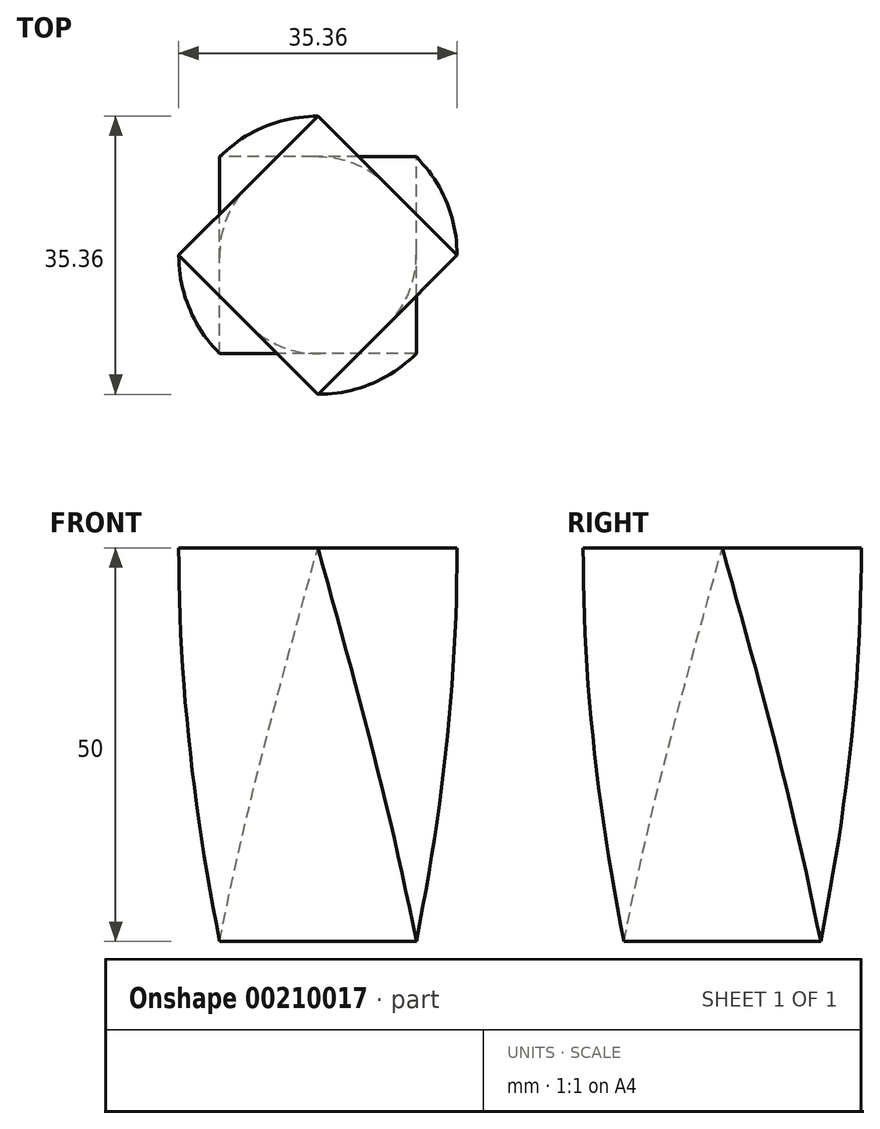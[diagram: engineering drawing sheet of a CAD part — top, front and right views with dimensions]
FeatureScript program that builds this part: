
annotation { "Feature Type Name" : "Feature", "Feature Type Description" : "" }
export const myFeature = defineFeature(function(context is Context, id is Id, definition is map)
    precondition{}
    {
        {
            assignVariable(context, id + "F0", {"name" : "p", "anyValue" : 10});
        }
        {
            var Q0;
            Q0=qCreatedBy(makeId("Top.planeOp"),FACE);
            cPlane(context, id + "F1", {"entities" : qUnion([Q0]), "cplaneType" : CPlaneType.OFFSET, "offset" : (getVariable(context, 'p')) * mm, "width" : 150 * mm, "height" : 150 * mm});
        }
        {
            var Q0;
            Q0=qCreatedBy(id+"F1.planeOp",FACE);
            cPlane(context, id + "F2", {"entities" : qUnion([Q0]), "cplaneType" : CPlaneType.OFFSET, "offset" : (getVariable(context, 'p')) * mm, "width" : 150 * mm, "height" : 150 * mm});
        }
        {
            var Q0;
            Q0=qCreatedBy(id+"F2.planeOp",FACE);
            cPlane(context, id + "F3", {"entities" : qUnion([Q0]), "cplaneType" : CPlaneType.OFFSET, "offset" : (getVariable(context, 'p')) * mm, "width" : 150 * mm, "height" : 150 * mm});
        }
        {
            var Q0;
            Q0=qCreatedBy(id+"F3.planeOp",FACE);
            cPlane(context, id + "F4", {"entities" : qUnion([Q0]), "cplaneType" : CPlaneType.OFFSET, "offset" : (getVariable(context, 'p')) * mm, "width" : 150 * mm, "height" : 150 * mm});
        }
        {
            var Q0;
            Q0=qCreatedBy(id+"F4.planeOp",FACE);
            cPlane(context, id + "F5", {"entities" : qUnion([Q0]), "cplaneType" : CPlaneType.OFFSET, "offset" : (getVariable(context, 'p')) * mm, "width" : 150 * mm, "height" : 150 * mm});
        }
        {
            var Q0;
            Q0=qCreatedBy(makeId("Top.planeOp"),FACE);
            var sketch = newSketch(context, id + "F6", { "sketchPlane" : qUnion([Q0])});
            skLineSegment(sketch, "E0.bottom", {"start": v(12.5, -12.5) * mm, "end": v(-12.5, -12.5) * mm});
            skLineSegment(sketch, "E0.top", {"start": v(12.5, 12.5) * mm, "end": v(-12.5, 12.5) * mm});
            skLineSegment(sketch, "E0.left", {"start": v(12.5, -12.5) * mm, "end": v(12.5, 12.5) * mm});
            skLineSegment(sketch, "E0.right", {"start": v(-12.5, -12.5) * mm, "end": v(-12.5, 12.5) * mm});
            skPoint(sketch, "E0.middle", {"position": v(0, 0) * mm});
            skSolve(sketch);
        }
        {
            var Q0;
            Q0=qCreatedBy(id+"F1.planeOp",FACE);
            var sketch = newSketch(context, id + "F7", { "sketchPlane" : qUnion([Q0])});
            skPoint(sketch, "E1.middle", {"position": v(0, 0) * mm});
            skLineSegment(sketch, "E2.1.1", {"start": v(10.4, -14.3) * mm, "end": v(-14.3, -10.4) * mm});
            skLineSegment(sketch, "E2.1.2", {"start": v(14.3, 10.4) * mm, "end": v(-10.4, 14.3) * mm});
            skLineSegment(sketch, "E2.1.3", {"start": v(10.4, -14.3) * mm, "end": v(14.3, 10.4) * mm});
            skLineSegment(sketch, "E2.1.4", {"start": v(-14.3, -10.4) * mm, "end": v(-10.4, 14.3) * mm});
            skSolve(sketch);
        }
        {
            var Q0;
            Q0=qCreatedBy(id+"F2.planeOp",FACE);
            var sketch = newSketch(context, id + "F8", { "sketchPlane" : qUnion([Q0])});
            skPoint(sketch, "E3.middle", {"position": v(0, 0) * mm});
            skLineSegment(sketch, "E4.1.0", {"start": v(15.75, 8.03) * mm, "end": v(-8.03, 15.75) * mm});
            skLineSegment(sketch, "E4.1.1", {"start": v(8.03, -15.75) * mm, "end": v(-15.75, -8.03) * mm});
            skLineSegment(sketch, "E4.1.2", {"start": v(8.03, -15.75) * mm, "end": v(15.75, 8.03) * mm});
            skLineSegment(sketch, "E4.1.3", {"start": v(-15.75, -8.03) * mm, "end": v(-8.03, 15.75) * mm});
            skSolve(sketch);
        }
        {
            var Q0;
            Q0=qCreatedBy(id+"F3.planeOp",FACE);
            var sketch = newSketch(context, id + "F9", { "sketchPlane" : qUnion([Q0])});
            skPoint(sketch, "E5.middle", {"position": v(0, 0) * mm});
            skLineSegment(sketch, "E6.1.0", {"start": v(16.81, 5.46) * mm, "end": v(-5.46, 16.81) * mm});
            skLineSegment(sketch, "E6.1.1", {"start": v(5.46, -16.81) * mm, "end": v(16.81, 5.46) * mm});
            skLineSegment(sketch, "E6.1.2", {"start": v(5.46, -16.81) * mm, "end": v(-16.81, -5.46) * mm});
            skLineSegment(sketch, "E6.1.4", {"start": v(-16.81, -5.46) * mm, "end": v(-5.46, 16.81) * mm});
            skSolve(sketch);
        }
        {
            var Q0;
            Q0=qCreatedBy(id+"F4.planeOp",FACE);
            var sketch = newSketch(context, id + "F10", { "sketchPlane" : qUnion([Q0])});
            skPoint(sketch, "E7.middle", {"position": v(0, 0) * mm});
            skLineSegment(sketch, "E8.1.0", {"start": v(2.77, -17.46) * mm, "end": v(17.46, 2.77) * mm});
            skLineSegment(sketch, "E8.1.1", {"start": v(17.46, 2.77) * mm, "end": v(-2.77, 17.46) * mm});
            skLineSegment(sketch, "E8.1.2", {"start": v(-17.46, -2.77) * mm, "end": v(-2.77, 17.46) * mm});
            skLineSegment(sketch, "E8.1.3", {"start": v(2.77, -17.46) * mm, "end": v(-17.46, -2.77) * mm});
            skSolve(sketch);
        }
        {
            var Q0;
            Q0=qCreatedBy(id+"F5.planeOp",FACE);
            var sketch = newSketch(context, id + "F11", { "sketchPlane" : qUnion([Q0])});
            skPoint(sketch, "E9.middle", {"position": v(0, 0) * mm});
            skLineSegment(sketch, "E10.1.0", {"start": v(-17.68, 0) * mm, "end": v(0, 17.68) * mm});
            skLineSegment(sketch, "E10.1.2", {"start": v(0, -17.68) * mm, "end": v(-17.68, 0) * mm});
            skLineSegment(sketch, "E10.1.3", {"start": v(17.68, 0) * mm, "end": v(0, 17.68) * mm});
            skLineSegment(sketch, "E10.1.4", {"start": v(0, -17.68) * mm, "end": v(17.68, 0) * mm});
            skSolve(sketch);
        }
        {
            var Q0;
            Q0=makeQuery(id+"F6.imprint","IMPRINT",FACE,{"disambiguationData":[TD([[makeQuery(id+"F6.imprint","IMPRINT",EDGE,{"derivedFrom":sQuery(id+"F6.wireOp",EDGE,"E0.bottom")}),-1.0]])]});
            var Q1;
            Q1=makeQuery(id+"F7.imprint","IMPRINT",FACE,{"disambiguationData":[TD([[makeQuery(id+"F7.imprint","IMPRINT",EDGE,{"derivedFrom":sQuery(id+"F7.wireOp",EDGE,"E2.1.1")}),-1.0]])]});
            var Q2;
            Q2=makeQuery(id+"F8.imprint","IMPRINT",FACE,{"disambiguationData":[TD([[makeQuery(id+"F8.imprint","IMPRINT",EDGE,{"derivedFrom":sQuery(id+"F8.wireOp",EDGE,"E4.1.0")}),1.0]])]});
            var Q3;
            Q3=makeQuery(id+"F9.imprint","IMPRINT",FACE,{"disambiguationData":[TD([[makeQuery(id+"F9.imprint","IMPRINT",EDGE,{"derivedFrom":sQuery(id+"F9.wireOp",EDGE,"E6.1.0")}),1.0]])]});
            var Q4;
            Q4=makeQuery(id+"F10.imprint","IMPRINT",FACE,{"disambiguationData":[TD([[makeQuery(id+"F10.imprint","IMPRINT",EDGE,{"derivedFrom":sQuery(id+"F10.wireOp",EDGE,"E8.1.0")}),1.0]])]});
            var Q5;
            Q5=makeQuery(id+"F11.imprint","IMPRINT",FACE,{"disambiguationData":[TD([[makeQuery(id+"F11.imprint","IMPRINT",EDGE,{"derivedFrom":sQuery(id+"F11.wireOp",EDGE,"E10.1.0")}),-1.0]])]});
            loft(context, id + "F12", {"sheetProfilesArray" : [{ "sheetProfileEntities" : qUnion([Q0]) }, { "sheetProfileEntities" : qUnion([Q1]) }, { "sheetProfileEntities" : qUnion([Q2]) }, { "sheetProfileEntities" : qUnion([Q3]) }, { "sheetProfileEntities" : qUnion([Q4]) }, { "sheetProfileEntities" : qUnion([Q5]) }]});
        }
    });
